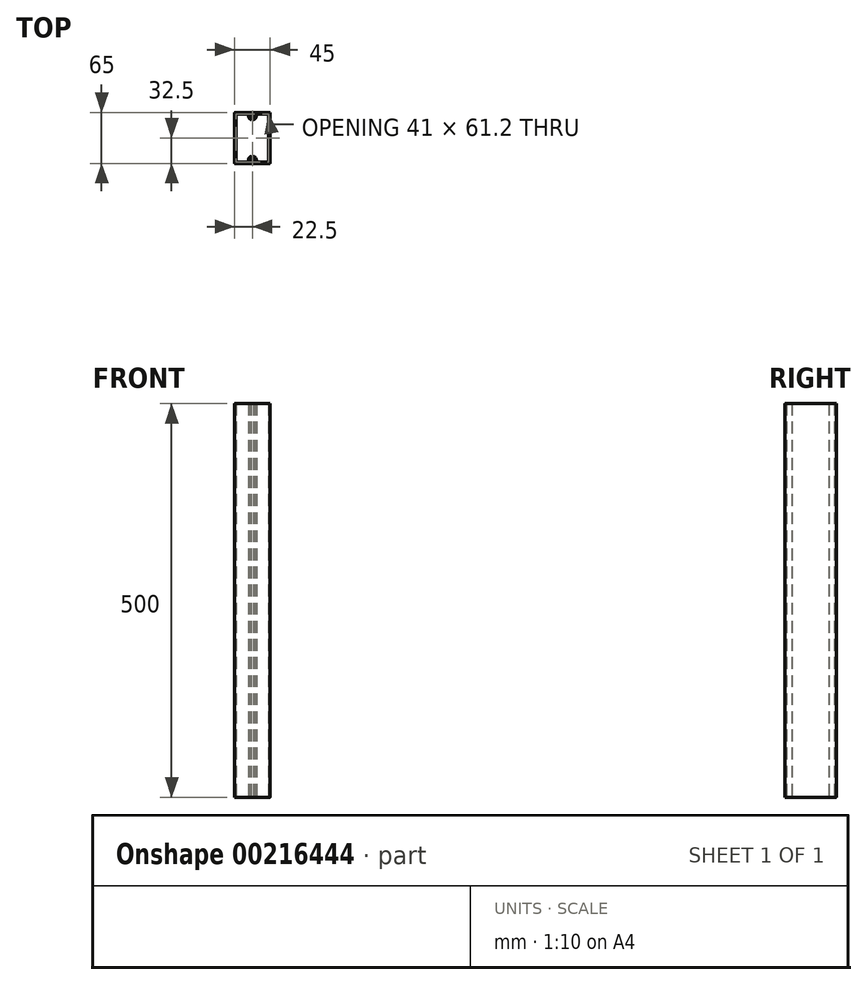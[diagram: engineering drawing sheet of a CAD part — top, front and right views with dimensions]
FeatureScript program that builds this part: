
annotation { "Feature Type Name" : "Feature", "Feature Type Description" : "" }
export const myFeature = defineFeature(function(context is Context, id is Id, definition is map)
    precondition{}
    {
        {
            var Q0;
            Q0=qCreatedBy(makeId("Top.planeOp"),FACE);
            var sketch = newSketch(context, id + "F0", { "sketchPlane" : qUnion([Q0])});
            skLineSegment(sketch, "E0.bottom", {"start": v(0.6, 0) * mm, "end": v(44.4, 0) * mm});
            skLineSegment(sketch, "E0.top", {"start": v(0.6, 65) * mm, "end": v(44.4, 65) * mm});
            skLineSegment(sketch, "E0.left", {"start": v(0, 0.6) * mm, "end": v(0, 64.4) * mm});
            skLineSegment(sketch, "E0.right", {"start": v(45, 0.6) * mm, "end": v(45, 64.4) * mm});
            skPoint(sketch, "E1.visualSharp", {"position": v(0, 65) * mm});
            skArc(sketch, "E1.filletArc", {"start": v(0.6, 65) * mm, "mid": v(0.18, 64.82) * mm, "end": v(0, 64.4) * mm});
            skPoint(sketch, "E2.visualSharp", {"position": v(45, 65) * mm});
            skArc(sketch, "E2.filletArc", {"start": v(45, 64.4) * mm, "mid": v(44.82, 64.82) * mm, "end": v(44.4, 65) * mm});
            skPoint(sketch, "E3.visualSharp", {"position": v(0, 0) * mm});
            skArc(sketch, "E3.filletArc", {"start": v(0, 0.6) * mm, "mid": v(0.18, 0.18) * mm, "end": v(0.6, 0) * mm});
            skPoint(sketch, "E4.visualSharp", {"position": v(45, 0) * mm});
            skArc(sketch, "E4.filletArc", {"start": v(44.4, 0) * mm, "mid": v(44.82, 0.18) * mm, "end": v(45, 0.6) * mm});
            skLineSegment(sketch, "E5.0", {"start": v(2, 2.5) * mm, "end": v(2, 62.5) * mm});
            skLineSegment(sketch, "E5.2", {"start": v(43, 2.5) * mm, "end": v(43, 62.5) * mm});
            skLineSegment(sketch, "E5.3", {"start": v(2.5, 63) * mm, "end": v(17, 63) * mm});
            skPoint(sketch, "E6.visualSharp", {"position": v(2, 63) * mm});
            skArc(sketch, "E6.filletArc", {"start": v(2.5, 63) * mm, "mid": v(2.15, 62.85) * mm, "end": v(2, 62.5) * mm});
            skPoint(sketch, "E7.visualSharp", {"position": v(43, 63) * mm});
            skArc(sketch, "E7.filletArc", {"start": v(43, 62.5) * mm, "mid": v(42.85, 62.85) * mm, "end": v(42.5, 63) * mm});
            skPoint(sketch, "E8.visualSharp", {"position": v(2, 2) * mm});
            skArc(sketch, "E8.filletArc", {"start": v(2, 2.5) * mm, "mid": v(2.15, 2.15) * mm, "end": v(2.5, 2) * mm});
            skPoint(sketch, "E9.visualSharp", {"position": v(43, 2) * mm});
            skArc(sketch, "E9.filletArc", {"start": v(42.5, 2) * mm, "mid": v(42.85, 2.15) * mm, "end": v(43, 2.5) * mm});
            skLineSegment(sketch, "E10", {"start": v(22.5, 65) * mm, "end": v(22.5, 0) * mm, "construction": true});
            skLineSegment(sketch, "E11", {"start": v(45, 32.5) * mm, "end": v(0, 32.5) * mm, "construction": true});
            skArc(sketch, "E12", {"start": v(17.5, 60.5) * mm, "mid": v(18.25, 57.86) * mm, "end": v(20.28, 56.02) * mm});
            skLineSegment(sketch, "E13", {"start": v(17.5, 60.5) * mm, "end": v(17.5, 62.5) * mm});
            skLineSegment(sketch, "E14", {"start": v(27.5, 60.5) * mm, "end": v(27.5, 62.5) * mm});
            skArc(sketch, "E15", {"start": v(24.18, 58.51) * mm, "mid": v(22.5, 63.1) * mm, "end": v(20.82, 58.51) * mm});
            skLineSegment(sketch, "E16", {"start": v(21, 58.13) * mm, "end": v(21, 56.47) * mm});
            skLineSegment(sketch, "E17.MirrorCS", {"start": v(24, 58.13) * mm, "end": v(24, 56.47) * mm});
            skLineSegment(sketch, "E18.trimOffspring", {"start": v(28, 63) * mm, "end": v(42.5, 63) * mm});
            skArc(sketch, "E19.trimOffspring", {"start": v(24.72, 56.02) * mm, "mid": v(26.75, 57.86) * mm, "end": v(27.5, 60.5) * mm});
            skPoint(sketch, "E20.visualSharp", {"position": v(17.5, 63) * mm});
            skArc(sketch, "E20.filletArc", {"start": v(17.5, 62.5) * mm, "mid": v(17.35, 62.85) * mm, "end": v(17, 63) * mm});
            skPoint(sketch, "E21.visualSharp", {"position": v(27.5, 63) * mm});
            skArc(sketch, "E21.filletArc", {"start": v(28, 63) * mm, "mid": v(27.65, 62.85) * mm, "end": v(27.5, 62.5) * mm});
            skPoint(sketch, "E22.visualSharp", {"position": v(24, 55.73) * mm});
            skArc(sketch, "E22.filletArc", {"start": v(24, 56.47) * mm, "mid": v(24.24, 56.04) * mm, "end": v(24.72, 56.02) * mm});
            skPoint(sketch, "E23.visualSharp", {"position": v(21, 55.73) * mm});
            skArc(sketch, "E23.filletArc", {"start": v(20.28, 56.02) * mm, "mid": v(20.76, 56.04) * mm, "end": v(21, 56.47) * mm});
            skPoint(sketch, "E24.visualSharp", {"position": v(21, 58.38) * mm});
            skArc(sketch, "E24.filletArc", {"start": v(21, 58.13) * mm, "mid": v(20.95, 58.34) * mm, "end": v(20.82, 58.51) * mm});
            skPoint(sketch, "E25.visualSharp", {"position": v(24, 58.38) * mm});
            skArc(sketch, "E25.filletArc", {"start": v(24.18, 58.51) * mm, "mid": v(24.05, 58.34) * mm, "end": v(24, 58.13) * mm});
            skArc(sketch, "E26.MirrorCS", {"start": v(21, 6.87) * mm, "mid": v(20.95, 6.66) * mm, "end": v(20.82, 6.49) * mm});
            skArc(sketch, "E27.MirrorCS", {"start": v(24.18, 6.49) * mm, "mid": v(24.05, 6.66) * mm, "end": v(24, 6.87) * mm});
            skArc(sketch, "E28.MirrorCS", {"start": v(20.28, 8.98) * mm, "mid": v(20.76, 8.96) * mm, "end": v(21, 8.53) * mm});
            skArc(sketch, "E29.MirrorCS", {"start": v(28, 2) * mm, "mid": v(27.65, 2.15) * mm, "end": v(27.5, 2.5) * mm});
            skLineSegment(sketch, "E30.MirrorCS", {"start": v(21, 6.87) * mm, "end": v(21, 8.53) * mm});
            skLineSegment(sketch, "E31.MirrorCS", {"start": v(24, 6.87) * mm, "end": v(24, 8.53) * mm});
            skArc(sketch, "E32.MirrorCS", {"start": v(17.5, 2.5) * mm, "mid": v(17.35, 2.15) * mm, "end": v(17, 2) * mm});
            skArc(sketch, "E33.MirrorCS", {"start": v(24, 8.53) * mm, "mid": v(24.24, 8.96) * mm, "end": v(24.72, 8.98) * mm});
            skPoint(sketch, "E34.MirrorP", {"position": v(24, 6.62) * mm});
            skLineSegment(sketch, "E35.MirrorCS", {"start": v(2.5, 2) * mm, "end": v(17, 2) * mm});
            skArc(sketch, "E36.MirrorCS", {"start": v(24.72, 8.98) * mm, "mid": v(26.75, 7.14) * mm, "end": v(27.5, 4.5) * mm});
            skPoint(sketch, "E37.MirrorP", {"position": v(21, 9.27) * mm});
            skArc(sketch, "E38.MirrorCS", {"start": v(17.5, 4.5) * mm, "mid": v(18.25, 7.14) * mm, "end": v(20.28, 8.98) * mm});
            skPoint(sketch, "E39.MirrorP", {"position": v(24, 9.27) * mm});
            skArc(sketch, "E40.MirrorCS", {"start": v(24.18, 6.49) * mm, "mid": v(22.5, 1.9) * mm, "end": v(20.82, 6.49) * mm});
            skLineSegment(sketch, "E41.MirrorCS", {"start": v(27.5, 4.5) * mm, "end": v(27.5, 2.5) * mm});
            skLineSegment(sketch, "E42.MirrorCS", {"start": v(22.5, 0) * mm, "end": v(22.5, 65) * mm, "construction": true});
            skLineSegment(sketch, "E43.MirrorCS", {"start": v(17.5, 4.5) * mm, "end": v(17.5, 2.5) * mm});
            skPoint(sketch, "E44.MirrorP", {"position": v(17.5, 2) * mm});
            skPoint(sketch, "E45.MirrorP", {"position": v(27.5, 2) * mm});
            skLineSegment(sketch, "E46.MirrorCS", {"start": v(28, 2) * mm, "end": v(42.5, 2) * mm});
            skPoint(sketch, "E47.MirrorP", {"position": v(21, 6.62) * mm});
            skSolve(sketch);
        }
        {
            var Q0;
            Q0=makeQuery(id+"F0.imprint","IMPRINT",FACE,{"disambiguationData":[TD([[makeQuery(id+"F0.imprint","IMPRINT",EDGE,{"derivedFrom":sQuery(id+"F0.wireOp",EDGE,"E0.bottom")}),1.0]])]});
            extrude(context, id + "F1", {"entities" : qUnion([Q0]), "depth" : 500 * mm});
        }
        {
            var Q0;
            Q0=makeQuery(id+"F1.opExtrude","CAP_FACE",FACE,{"disambiguationData":[OSD([sQuery(id+"F0.wireOp",EDGE,"E0.bottom"),sQuery(id+"F0.wireOp",EDGE,"E0.top"),sQuery(id+"F0.wireOp",EDGE,"E0.left"),sQuery(id+"F0.wireOp",EDGE,"E0.right"),sQuery(id+"F0.wireOp",EDGE,"E1.filletArc"),sQuery(id+"F0.wireOp",EDGE,"E2.filletArc"),sQuery(id+"F0.wireOp",EDGE,"E3.filletArc"),sQuery(id+"F0.wireOp",EDGE,"E4.filletArc"),sQuery(id+"F0.wireOp",EDGE,"E5.0"),sQuery(id+"F0.wireOp",EDGE,"E5.2"),sQuery(id+"F0.wireOp",EDGE,"E5.3"),sQuery(id+"F0.wireOp",EDGE,"E6.filletArc"),sQuery(id+"F0.wireOp",EDGE,"E7.filletArc"),sQuery(id+"F0.wireOp",EDGE,"E8.filletArc"),sQuery(id+"F0.wireOp",EDGE,"E9.filletArc"),sQuery(id+"F0.wireOp",EDGE,"E12"),sQuery(id+"F0.wireOp",EDGE,"E13"),sQuery(id+"F0.wireOp",EDGE,"E14"),sQuery(id+"F0.wireOp",EDGE,"E15"),sQuery(id+"F0.wireOp",EDGE,"E16"),sQuery(id+"F0.wireOp",EDGE,"E17.MirrorCS"),sQuery(id+"F0.wireOp",EDGE,"E18.trimOffspring"),sQuery(id+"F0.wireOp",EDGE,"E19.trimOffspring"),sQuery(id+"F0.wireOp",EDGE,"E20.filletArc"),sQuery(id+"F0.wireOp",EDGE,"E21.filletArc"),sQuery(id+"F0.wireOp",EDGE,"E22.filletArc"),sQuery(id+"F0.wireOp",EDGE,"E23.filletArc"),sQuery(id+"F0.wireOp",EDGE,"E24.filletArc"),sQuery(id+"F0.wireOp",EDGE,"E25.filletArc"),sQuery(id+"F0.wireOp",EDGE,"E26.MirrorCS"),sQuery(id+"F0.wireOp",EDGE,"E27.MirrorCS"),sQuery(id+"F0.wireOp",EDGE,"E28.MirrorCS"),sQuery(id+"F0.wireOp",EDGE,"E29.MirrorCS"),sQuery(id+"F0.wireOp",EDGE,"E30.MirrorCS"),sQuery(id+"F0.wireOp",EDGE,"E31.MirrorCS"),sQuery(id+"F0.wireOp",EDGE,"E32.MirrorCS"),sQuery(id+"F0.wireOp",EDGE,"E33.MirrorCS"),sQuery(id+"F0.wireOp",EDGE,"E35.MirrorCS"),sQuery(id+"F0.wireOp",EDGE,"E36.MirrorCS"),sQuery(id+"F0.wireOp",EDGE,"E38.MirrorCS"),sQuery(id+"F0.wireOp",EDGE,"E40.MirrorCS"),sQuery(id+"F0.wireOp",EDGE,"E41.MirrorCS"),sQuery(id+"F0.wireOp",EDGE,"E43.MirrorCS"),sQuery(id+"F0.wireOp",EDGE,"E46.MirrorCS")])],"isStart":true});
            var sketch = newSketch(context, id + "F2", { "sketchPlane" : qUnion([Q0])});
            skLineSegment(sketch, "E48", {"start": v(22.5, -1.9) * mm, "end": v(22.5, -63.1) * mm, "construction": true});
            skLineSegment(sketch, "E49", {"start": v(2, -32.5) * mm, "end": v(43, -32.5) * mm, "construction": true});
            skSolve(sketch);
        }
    });
